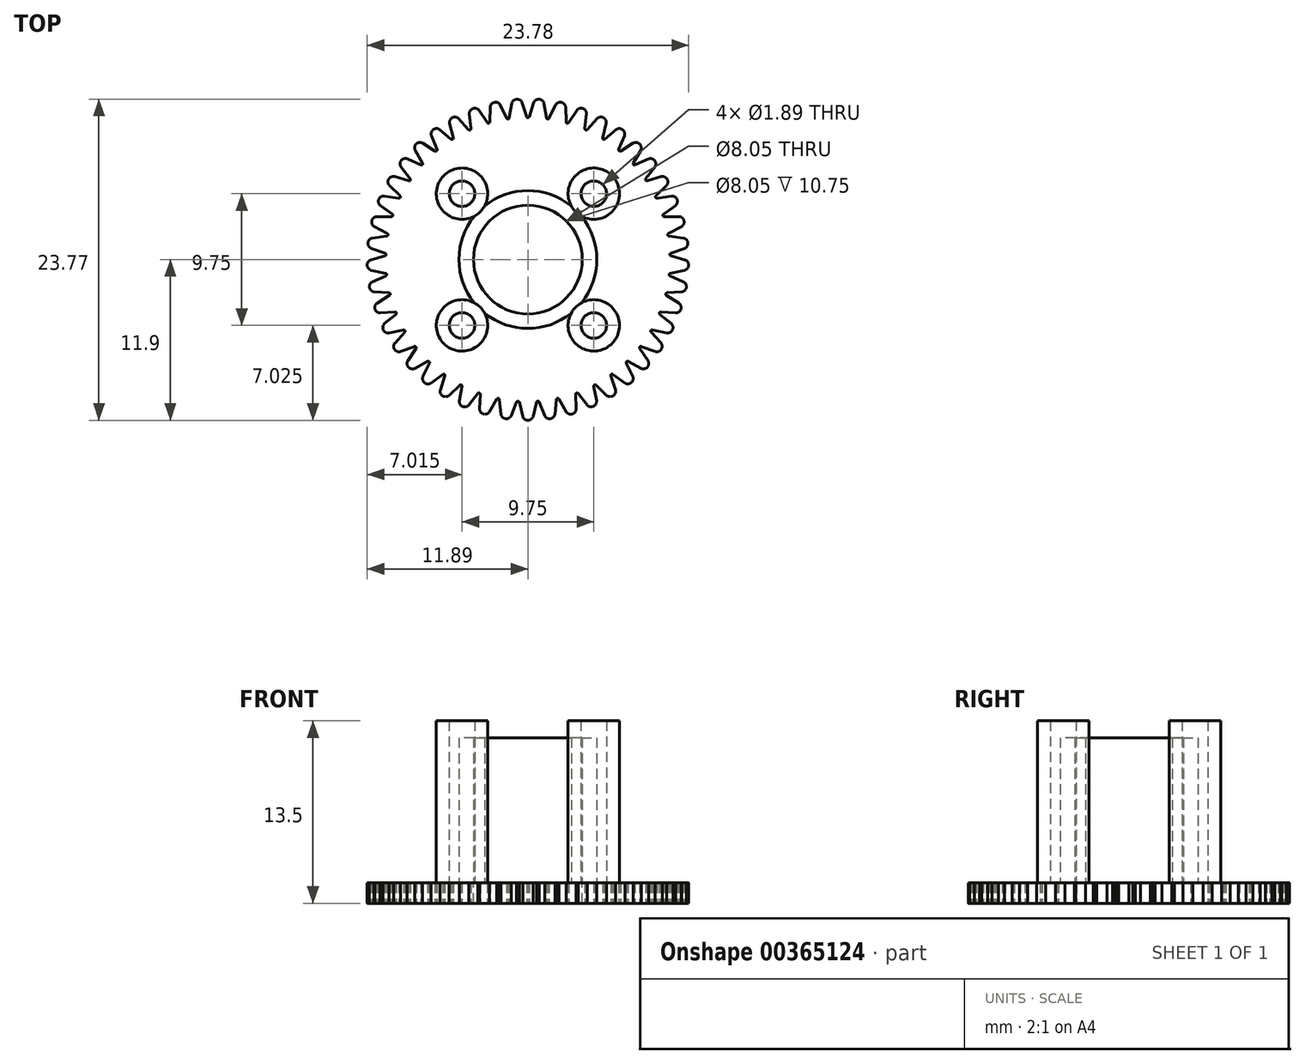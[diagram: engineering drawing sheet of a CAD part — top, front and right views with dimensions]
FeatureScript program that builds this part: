
annotation { "Feature Type Name" : "Feature", "Feature Type Description" : "" }
export const myFeature = defineFeature(function(context is Context, id is Id, definition is map)
    precondition{}
    {
        {
            var Q0;
            Q0=qCreatedBy(makeId("Top.planeOp"),FACE);
            var sketch = newSketch(context, id + "F0", { "sketchPlane" : qUnion([Q0])});
            skLineSegment(sketch, "E0.bottom", {"start": v(-6.77, 6.78) * mm, "end": v(6.78, 6.78) * mm});
            skLineSegment(sketch, "E0.top", {"start": v(-6.78, -6.78) * mm, "end": v(6.77, -6.78) * mm});
            skLineSegment(sketch, "E0.left", {"start": v(-6.77, 6.78) * mm, "end": v(-6.78, -6.78) * mm});
            skLineSegment(sketch, "E0.right", {"start": v(6.78, 6.78) * mm, "end": v(6.77, -6.78) * mm});
            skPoint(sketch, "E0.middle", {"position": v(0, 0) * mm});
            skCircle(sketch, "E1", {"center": v(-4.88, -4.88) * mm, "radius": 1.9 * mm});
            skCircle(sketch, "E2", {"center": v(-4.88, 4.88) * mm, "radius": 1.9 * mm});
            skCircle(sketch, "E3", {"center": v(4.88, 4.88) * mm, "radius": 1.9 * mm});
            skCircle(sketch, "E4", {"center": v(4.88, -4.88) * mm, "radius": 1.9 * mm});
            skCircle(sketch, "E5", {"center": v(0, 0) * mm, "radius": 5.1 * mm});
            skCircle(sketch, "E6", {"center": v(0, 0) * mm, "radius": 4.03 * mm});
            skCircle(sketch, "E7", {"center": v(-4.88, -4.88) * mm, "radius": 0.94 * mm});
            skCircle(sketch, "E8", {"center": v(-4.88, 4.88) * mm, "radius": 0.94 * mm});
            skCircle(sketch, "E9", {"center": v(4.88, 4.88) * mm, "radius": 0.94 * mm});
            skCircle(sketch, "E10", {"center": v(4.88, -4.88) * mm, "radius": 0.94 * mm});
            skSolve(sketch);
        }
        {
            var Q0;
            Q0=makeQuery(id+"F0.imprint","IMPRINT",FACE,{"disambiguationData":[TD([[makeQuery(id+"F0.imprint","IMPRINT",EDGE,{"derivedFrom":sQuery(id+"F0.wireOp",EDGE,"E8")}),-1.0]])]});
            var Q1;
            Q1=makeQuery(id+"F0.imprint","IMPRINT",FACE,{"disambiguationData":[TD([[makeQuery(id+"F0.imprint","IMPRINT",EDGE,{"derivedFrom":sQuery(id+"F0.wireOp",EDGE,"E9")}),-1.0]])]});
            var Q2;
            Q2=makeQuery(id+"F0.imprint","IMPRINT",FACE,{"disambiguationData":[TD([[makeQuery(id+"F0.imprint","IMPRINT",EDGE,{"derivedFrom":sQuery(id+"F0.wireOp",EDGE,"E10")}),-1.0]])]});
            var Q3;
            Q3=makeQuery(id+"F0.imprint","IMPRINT",FACE,{"disambiguationData":[TD([[makeQuery(id+"F0.imprint","IMPRINT",EDGE,{"derivedFrom":sQuery(id+"F0.wireOp",EDGE,"E7")}),-1.0]])]});
            var Q4;
            Q4=makeQuery(id+"F0.imprint","IMPRINT",FACE,{"disambiguationData":[TD([[makeQuery(id+"F0.imprint","IMPRINT",EDGE,{"derivedFrom":sQuery(id+"F0.wireOp",EDGE,"E6")}),-1.0]])]});
            var Q5;
            {var subQ0=sQuery(id+"F0.wireOp",EDGE,"E5");var subQ1=sQuery(id+"F0.wireOp",EDGE,"E2");var subQ2=makeQuery(id+"F0.imprint","INTERSECT",VERTEX,{"disambiguationData":[OD(0.0)],"derivedFrom":[subQ1,subQ0]});Q5=makeQuery(id+"F0.imprint","IMPRINT",FACE,{"disambiguationData":[TD([[makeQuery(id+"F0.imprint","IMPRINT",EDGE,{"disambiguationData":[TD([[subQ2,-1.0]])],"derivedFrom":subQ1}),1.0]])]});}
            var Q6;
            {var subQ0=sQuery(id+"F0.wireOp",EDGE,"E5");var subQ1=sQuery(id+"F0.wireOp",EDGE,"E3");var subQ2=makeQuery(id+"F0.imprint","INTERSECT",VERTEX,{"disambiguationData":[OD(0.0)],"derivedFrom":[subQ1,subQ0]});Q6=makeQuery(id+"F0.imprint","IMPRINT",FACE,{"disambiguationData":[TD([[makeQuery(id+"F0.imprint","IMPRINT",EDGE,{"disambiguationData":[TD([[subQ2,-1.0]])],"derivedFrom":subQ1}),1.0]])]});}
            var Q7;
            {var subQ0=sQuery(id+"F0.wireOp",EDGE,"E5");var subQ1=sQuery(id+"F0.wireOp",EDGE,"E4");var subQ2=makeQuery(id+"F0.imprint","INTERSECT",VERTEX,{"disambiguationData":[OD(0.0)],"derivedFrom":[subQ1,subQ0]});Q7=makeQuery(id+"F0.imprint","IMPRINT",FACE,{"disambiguationData":[TD([[makeQuery(id+"F0.imprint","IMPRINT",EDGE,{"disambiguationData":[TD([[subQ2,-1.0]])],"derivedFrom":subQ1}),1.0]])]});}
            var Q8;
            {var subQ0=sQuery(id+"F0.wireOp",EDGE,"E5");var subQ1=sQuery(id+"F0.wireOp",EDGE,"E1");var subQ2=makeQuery(id+"F0.imprint","INTERSECT",VERTEX,{"disambiguationData":[OD(0.0)],"derivedFrom":[subQ1,subQ0]});Q8=makeQuery(id+"F0.imprint","IMPRINT",FACE,{"disambiguationData":[TD([[makeQuery(id+"F0.imprint","IMPRINT",EDGE,{"disambiguationData":[TD([[subQ2,1.0]])],"derivedFrom":subQ1}),1.0]])]});}
            extrude(context, id + "F1", {"entities" : qUnion([Q0, Q1, Q2, Q3, Q4, Q5, Q6, Q7, Q8]), "depth" : 12 * mm});
        }
        {
            var Q0;
            Q0=makeQuery(id+"F1.opExtrude","CAP_FACE",FACE,{"disambiguationData":[OSD([sQuery(id+"F0.wireOp",EDGE,"E1"),sQuery(id+"F0.wireOp",EDGE,"E2"),sQuery(id+"F0.wireOp",EDGE,"E3"),sQuery(id+"F0.wireOp",EDGE,"E4"),sQuery(id+"F0.wireOp",EDGE,"E5"),sQuery(id+"F0.wireOp",EDGE,"E6")])],"isStart":true});
            var sketch = newSketch(context, id + "F2", { "sketchPlane" : qUnion([Q0])});
            skCircle(sketch, "E11", {"center": v(0, 0) * mm, "radius": 11.9 * mm});
            skSolve(sketch);
        }
        {
            var Q0;
            Q0 = qSketchRegion(id + "F2", true);
            extrude(context, id + "F3", {"entities" : qUnion([Q0]), "depth" : 1.5 * mm});
        }
        {
            var Q0;
            Q0=makeQuery(id+"F3.opExtrude","CAP_FACE",FACE,{"disambiguationData":[OSD([sQuery(id+"F2.wireOp",EDGE,"E11")])],"isStart":false});
            var sketch = newSketch(context, id + "F4", { "sketchPlane" : qUnion([Q0])});
            skLineSegment(sketch, "E12", {"start": v(-0.75, 10.47) * mm, "end": v(0.75, 10.47) * mm});
            skPoint(sketch, "E13", {"position": v(0, 10.47) * mm});
            skLineSegment(sketch, "E14", {"start": v(-0.4, 11.47) * mm, "end": v(0.4, 11.47) * mm});
            skPoint(sketch, "E15", {"position": v(0, 11.47) * mm});
            skArc(sketch, "E16", {"start": v(0.38, 11.62) * mm, "mid": v(0, 11.9) * mm, "end": v(-0.38, 11.62) * mm});
            skLineSegment(sketch, "E17.MirrorCS", {"start": v(0.64, 10.56) * mm, "end": v(0.38, 11.62) * mm});
            skLineSegment(sketch, "E18.MirrorCS", {"start": v(-0.64, 10.56) * mm, "end": v(-0.38, 11.62) * mm});
            skCircle(sketch, "E19.0", {"center": v(0, 0) * mm, "radius": 11.9 * mm});
            skCircle(sketch, "E20", {"center": v(0, 0) * mm, "radius": 12.27 * mm});
            skLineSegment(sketch, "E21", {"start": v(0, 0) * mm, "end": v(0, 10.47) * mm});
            skArc(sketch, "E22.MirrorCS", {"start": v(0.75, 10.47) * mm, "mid": v(0.68, 10.5) * mm, "end": v(0.64, 10.56) * mm});
            skArc(sketch, "E23", {"start": v(-0.75, 10.47) * mm, "mid": v(-0.67, 10.5) * mm, "end": v(-0.63, 10.58) * mm});
            skArc(sketch, "E24.1.0", {"start": v(-1.24, 11.56) * mm, "mid": v(-1.65, 11.78) * mm, "end": v(-2, 11.45) * mm});
            skLineSegment(sketch, "E24.1.1", {"start": v(-2.1, 10.37) * mm, "end": v(-2, 11.45) * mm});
            skLineSegment(sketch, "E24.1.2", {"start": v(-0.84, 10.55) * mm, "end": v(-1.24, 11.56) * mm});
            skArc(sketch, "E24.1.3", {"start": v(-2.2, 10.27) * mm, "mid": v(-2.13, 10.3) * mm, "end": v(-2.1, 10.39) * mm});
            skArc(sketch, "E24.1.4", {"start": v(-0.71, 10.48) * mm, "mid": v(-0.79, 10.5) * mm, "end": v(-0.84, 10.55) * mm});
            skArc(sketch, "E24.2.0", {"start": v(-2.84, 11.27) * mm, "mid": v(-3.28, 11.44) * mm, "end": v(-3.57, 11.07) * mm});
            skLineSegment(sketch, "E24.2.1", {"start": v(-3.53, 9.98) * mm, "end": v(-3.57, 11.07) * mm});
            skLineSegment(sketch, "E24.2.2", {"start": v(-2.3, 10.33) * mm, "end": v(-2.84, 11.27) * mm});
            skArc(sketch, "E24.2.3", {"start": v(-3.6, 9.86) * mm, "mid": v(-3.54, 9.91) * mm, "end": v(-3.53, 10) * mm});
            skArc(sketch, "E24.2.4", {"start": v(-2.17, 10.27) * mm, "mid": v(-2.24, 10.28) * mm, "end": v(-2.3, 10.33) * mm});
            skArc(sketch, "E24.3.0", {"start": v(-4.38, 10.77) * mm, "mid": v(-4.84, 10.87) * mm, "end": v(-5.07, 10.46) * mm});
            skLineSegment(sketch, "E24.3.1", {"start": v(-4.88, 9.39) * mm, "end": v(-5.07, 10.46) * mm});
            skLineSegment(sketch, "E24.3.2", {"start": v(-3.71, 9.9) * mm, "end": v(-4.38, 10.77) * mm});
            skArc(sketch, "E24.3.3", {"start": v(-4.95, 9.26) * mm, "mid": v(-4.89, 9.32) * mm, "end": v(-4.88, 9.4) * mm});
            skArc(sketch, "E24.3.4", {"start": v(-3.57, 9.87) * mm, "mid": v(-3.65, 9.87) * mm, "end": v(-3.71, 9.9) * mm});
            skArc(sketch, "E24.4.0", {"start": v(-5.83, 10.06) * mm, "mid": v(-6.3, 10.1) * mm, "end": v(-6.48, 9.65) * mm});
            skLineSegment(sketch, "E24.4.1", {"start": v(-6.14, 8.62) * mm, "end": v(-6.48, 9.65) * mm});
            skLineSegment(sketch, "E24.4.2", {"start": v(-5.05, 9.3) * mm, "end": v(-5.83, 10.06) * mm});
            skArc(sketch, "E24.4.3", {"start": v(-6.19, 8.48) * mm, "mid": v(-6.14, 8.55) * mm, "end": v(-6.14, 8.63) * mm});
            skArc(sketch, "E24.4.4", {"start": v(-4.91, 9.28) * mm, "mid": v(-4.99, 9.27) * mm, "end": v(-5.05, 9.3) * mm});
            skArc(sketch, "E24.5.0", {"start": v(-7.18, 9.15) * mm, "mid": v(-7.65, 9.11) * mm, "end": v(-7.76, 8.66) * mm});
            skLineSegment(sketch, "E24.5.1", {"start": v(-7.28, 7.68) * mm, "end": v(-7.76, 8.66) * mm});
            skLineSegment(sketch, "E24.5.2", {"start": v(-6.3, 8.5) * mm, "end": v(-7.18, 9.15) * mm});
            skArc(sketch, "E24.5.3", {"start": v(-7.3, 7.54) * mm, "mid": v(-7.27, 7.61) * mm, "end": v(-7.29, 7.7) * mm});
            skArc(sketch, "E24.5.4", {"start": v(-6.16, 8.5) * mm, "mid": v(-6.23, 8.48) * mm, "end": v(-6.3, 8.5) * mm});
            skArc(sketch, "E24.6.0", {"start": v(-8.38, 8.06) * mm, "mid": v(-8.84, 7.96) * mm, "end": v(-8.9, 7.5) * mm});
            skLineSegment(sketch, "E24.6.1", {"start": v(-8.28, 6.6) * mm, "end": v(-8.9, 7.5) * mm});
            skLineSegment(sketch, "E24.6.2", {"start": v(-7.42, 7.54) * mm, "end": v(-8.38, 8.06) * mm});
            skArc(sketch, "E24.6.3", {"start": v(-8.29, 6.45) * mm, "mid": v(-8.26, 6.53) * mm, "end": v(-8.29, 6.6) * mm});
            skArc(sketch, "E24.6.4", {"start": v(-7.28, 7.57) * mm, "mid": v(-7.35, 7.53) * mm, "end": v(-7.42, 7.54) * mm});
            skArc(sketch, "E24.7.0", {"start": v(-9.42, 6.81) * mm, "mid": v(-9.86, 6.65) * mm, "end": v(-9.85, 6.18) * mm});
            skLineSegment(sketch, "E24.7.1", {"start": v(-9.11, 5.38) * mm, "end": v(-9.85, 6.18) * mm});
            skLineSegment(sketch, "E24.7.2", {"start": v(-8.4, 6.44) * mm, "end": v(-9.42, 6.81) * mm});
            skArc(sketch, "E24.7.3", {"start": v(-9.1, 5.24) * mm, "mid": v(-9.09, 5.32) * mm, "end": v(-9.12, 5.39) * mm});
            skArc(sketch, "E24.7.4", {"start": v(-8.26, 6.48) * mm, "mid": v(-8.32, 6.44) * mm, "end": v(-8.4, 6.44) * mm});
            skArc(sketch, "E24.8.0", {"start": v(-10.28, 5.44) * mm, "mid": v(-10.7, 5.22) * mm, "end": v(-10.61, 4.75) * mm});
            skLineSegment(sketch, "E24.8.1", {"start": v(-9.77, 4.06) * mm, "end": v(-10.61, 4.75) * mm});
            skLineSegment(sketch, "E24.8.2", {"start": v(-9.21, 5.2) * mm, "end": v(-10.28, 5.44) * mm});
            skArc(sketch, "E24.8.3", {"start": v(-9.74, 3.92) * mm, "mid": v(-9.74, 4) * mm, "end": v(-9.79, 4.07) * mm});
            skArc(sketch, "E24.8.4", {"start": v(-9.09, 5.27) * mm, "mid": v(-9.14, 5.22) * mm, "end": v(-9.21, 5.2) * mm});
            skArc(sketch, "E24.9.0", {"start": v(-10.93, 3.95) * mm, "mid": v(-11.32, 3.68) * mm, "end": v(-11.17, 3.23) * mm});
            skLineSegment(sketch, "E24.9.1", {"start": v(-10.24, 2.66) * mm, "end": v(-11.17, 3.23) * mm});
            skLineSegment(sketch, "E24.9.2", {"start": v(-9.85, 3.87) * mm, "end": v(-10.93, 3.95) * mm});
            skArc(sketch, "E24.9.3", {"start": v(-10.2, 2.52) * mm, "mid": v(-10.2, 2.6) * mm, "end": v(-10.26, 2.66) * mm});
            skArc(sketch, "E24.9.4", {"start": v(-9.73, 3.95) * mm, "mid": v(-9.78, 3.9) * mm, "end": v(-9.85, 3.87) * mm});
            skArc(sketch, "E24.10.0", {"start": v(-11.38, 2.4) * mm, "mid": v(-11.72, 2.07) * mm, "end": v(-11.51, 1.64) * mm});
            skLineSegment(sketch, "E24.10.1", {"start": v(-10.51, 1.2) * mm, "end": v(-11.51, 1.64) * mm});
            skLineSegment(sketch, "E24.10.2", {"start": v(-10.29, 2.46) * mm, "end": v(-11.38, 2.4) * mm});
            skArc(sketch, "E24.10.3", {"start": v(-10.44, 1.08) * mm, "mid": v(-10.46, 1.16) * mm, "end": v(-10.53, 1.21) * mm});
            skArc(sketch, "E24.10.4", {"start": v(-10.18, 2.56) * mm, "mid": v(-10.22, 2.5) * mm, "end": v(-10.29, 2.46) * mm});
            skArc(sketch, "E24.11.0", {"start": v(-11.6, 0.79) * mm, "mid": v(-11.9, 0.42) * mm, "end": v(-11.63, 0.02) * mm});
            skLineSegment(sketch, "E24.11.1", {"start": v(-10.58, -0.27) * mm, "end": v(-11.63, 0.02) * mm});
            skLineSegment(sketch, "E24.11.2", {"start": v(-10.53, 1) * mm, "end": v(-11.6, 0.79) * mm});
            skArc(sketch, "E24.11.3", {"start": v(-10.5, -0.38) * mm, "mid": v(-10.52, -0.3) * mm, "end": v(-10.6, -0.27) * mm});
            skArc(sketch, "E24.11.4", {"start": v(-10.44, 1.12) * mm, "mid": v(-10.47, 1.05) * mm, "end": v(-10.53, 1) * mm});
            skArc(sketch, "E24.12.0", {"start": v(-11.6, -0.83) * mm, "mid": v(-11.83, -1.24) * mm, "end": v(-11.52, -1.6) * mm});
            skLineSegment(sketch, "E24.12.1", {"start": v(-10.44, -1.74) * mm, "end": v(-11.52, -1.6) * mm});
            skLineSegment(sketch, "E24.12.2", {"start": v(-10.57, -0.47) * mm, "end": v(-11.6, -0.83) * mm});
            skArc(sketch, "E24.12.3", {"start": v(-10.34, -1.84) * mm, "mid": v(-10.38, -1.77) * mm, "end": v(-10.45, -1.74) * mm});
            skArc(sketch, "E24.12.4", {"start": v(-10.5, -0.35) * mm, "mid": v(-10.51, -0.42) * mm, "end": v(-10.57, -0.47) * mm});
            skArc(sketch, "E24.13.0", {"start": v(-11.37, -2.44) * mm, "mid": v(-11.54, -2.88) * mm, "end": v(-11.18, -3.18) * mm});
            skLineSegment(sketch, "E24.13.1", {"start": v(-10.1, -3.17) * mm, "end": v(-11.18, -3.18) * mm});
            skLineSegment(sketch, "E24.13.2", {"start": v(-10.4, -1.93) * mm, "end": v(-11.37, -2.44) * mm});
            skArc(sketch, "E24.13.3", {"start": v(-9.98, -3.26) * mm, "mid": v(-10.03, -3.2) * mm, "end": v(-10.1, -3.17) * mm});
            skArc(sketch, "E24.13.4", {"start": v(-10.34, -1.8) * mm, "mid": v(-10.35, -1.88) * mm, "end": v(-10.4, -1.93) * mm});
            skArc(sketch, "E24.14.0", {"start": v(-10.92, -4) * mm, "mid": v(-11.03, -4.46) * mm, "end": v(-10.63, -4.7) * mm});
            skLineSegment(sketch, "E24.14.1", {"start": v(-9.55, -4.55) * mm, "end": v(-10.63, -4.7) * mm});
            skLineSegment(sketch, "E24.14.2", {"start": v(-10.03, -3.36) * mm, "end": v(-10.92, -4) * mm});
            skArc(sketch, "E24.14.3", {"start": v(-9.43, -4.62) * mm, "mid": v(-9.49, -4.56) * mm, "end": v(-9.57, -4.55) * mm});
            skArc(sketch, "E24.14.4", {"start": v(-10, -3.23) * mm, "mid": v(-10, -3.3) * mm, "end": v(-10.03, -3.36) * mm});
            skArc(sketch, "E24.15.0", {"start": v(-10.25, -5.48) * mm, "mid": v(-10.3, -5.95) * mm, "end": v(-9.87, -6.14) * mm});
            skLineSegment(sketch, "E24.15.1", {"start": v(-8.83, -5.83) * mm, "end": v(-9.87, -6.14) * mm});
            skLineSegment(sketch, "E24.15.2", {"start": v(-9.47, -4.73) * mm, "end": v(-10.25, -5.48) * mm});
            skArc(sketch, "E24.15.3", {"start": v(-8.7, -5.89) * mm, "mid": v(-8.76, -5.84) * mm, "end": v(-8.84, -5.84) * mm});
            skArc(sketch, "E24.15.4", {"start": v(-9.45, -4.59) * mm, "mid": v(-9.43, -4.66) * mm, "end": v(-9.47, -4.73) * mm});
            skArc(sketch, "E24.16.0", {"start": v(-9.4, -6.85) * mm, "mid": v(-9.38, -7.32) * mm, "end": v(-8.92, -7.45) * mm});
            skLineSegment(sketch, "E24.16.1", {"start": v(-7.93, -7) * mm, "end": v(-8.92, -7.45) * mm});
            skLineSegment(sketch, "E24.16.2", {"start": v(-8.72, -6) * mm, "end": v(-9.4, -6.85) * mm});
            skArc(sketch, "E24.16.3", {"start": v(-7.8, -7.04) * mm, "mid": v(-7.86, -7) * mm, "end": v(-7.94, -7.01) * mm});
            skArc(sketch, "E24.16.4", {"start": v(-8.72, -5.86) * mm, "mid": v(-8.7, -5.93) * mm, "end": v(-8.72, -6) * mm});
            skArc(sketch, "E24.17.0", {"start": v(-8.35, -8.1) * mm, "mid": v(-8.27, -8.56) * mm, "end": v(-7.8, -8.62) * mm});
            skLineSegment(sketch, "E24.17.1", {"start": v(-6.88, -8.04) * mm, "end": v(-7.8, -8.62) * mm});
            skLineSegment(sketch, "E24.17.2", {"start": v(-7.8, -7.15) * mm, "end": v(-8.35, -8.1) * mm});
            skArc(sketch, "E24.17.3", {"start": v(-6.74, -8.06) * mm, "mid": v(-6.81, -8.03) * mm, "end": v(-6.9, -8.05) * mm});
            skArc(sketch, "E24.17.4", {"start": v(-7.82, -7.01) * mm, "mid": v(-7.78, -7.08) * mm, "end": v(-7.8, -7.15) * mm});
            skArc(sketch, "E24.18.0", {"start": v(-7.14, -9.18) * mm, "mid": v(-7, -9.63) * mm, "end": v(-6.52, -9.63) * mm});
            skLineSegment(sketch, "E24.18.1", {"start": v(-5.7, -8.92) * mm, "end": v(-6.52, -9.63) * mm});
            skLineSegment(sketch, "E24.18.2", {"start": v(-6.72, -8.17) * mm, "end": v(-7.14, -9.18) * mm});
            skArc(sketch, "E24.18.3", {"start": v(-5.55, -8.91) * mm, "mid": v(-5.63, -8.9) * mm, "end": v(-5.7, -8.93) * mm});
            skArc(sketch, "E24.18.4", {"start": v(-6.76, -8.03) * mm, "mid": v(-6.72, -8.1) * mm, "end": v(-6.72, -8.17) * mm});
            skArc(sketch, "E24.19.0", {"start": v(-5.8, -10.08) * mm, "mid": v(-5.59, -10.5) * mm, "end": v(-5.12, -10.44) * mm});
            skLineSegment(sketch, "E24.19.1", {"start": v(-4.4, -9.62) * mm, "end": v(-5.12, -10.44) * mm});
            skLineSegment(sketch, "E24.19.2", {"start": v(-5.52, -9.02) * mm, "end": v(-5.8, -10.08) * mm});
            skArc(sketch, "E24.19.3", {"start": v(-4.25, -9.6) * mm, "mid": v(-4.34, -9.6) * mm, "end": v(-4.4, -9.64) * mm});
            skArc(sketch, "E24.19.4", {"start": v(-5.58, -8.9) * mm, "mid": v(-5.53, -8.95) * mm, "end": v(-5.52, -9.02) * mm});
            skArc(sketch, "E24.20.0", {"start": v(-4.33, -10.79) * mm, "mid": v(-4.07, -11.18) * mm, "end": v(-3.62, -11.05) * mm});
            skLineSegment(sketch, "E24.20.1", {"start": v(-3.01, -10.14) * mm, "end": v(-3.62, -11.05) * mm});
            skLineSegment(sketch, "E24.20.2", {"start": v(-4.21, -9.7) * mm, "end": v(-4.33, -10.79) * mm});
            skArc(sketch, "E24.20.3", {"start": v(-2.88, -10.1) * mm, "mid": v(-2.96, -10.1) * mm, "end": v(-3.02, -10.16) * mm});
            skArc(sketch, "E24.20.4", {"start": v(-4.29, -9.59) * mm, "mid": v(-4.23, -9.63) * mm, "end": v(-4.21, -9.7) * mm});
            skArc(sketch, "E24.21.0", {"start": v(-2.79, -11.29) * mm, "mid": v(-2.47, -11.64) * mm, "end": v(-2.04, -11.45) * mm});
            skLineSegment(sketch, "E24.21.1", {"start": v(-1.57, -10.46) * mm, "end": v(-2.04, -11.45) * mm});
            skLineSegment(sketch, "E24.21.2", {"start": v(-2.82, -10.2) * mm, "end": v(-2.79, -11.29) * mm});
            skArc(sketch, "E24.21.3", {"start": v(-1.44, -10.4) * mm, "mid": v(-1.52, -10.42) * mm, "end": v(-1.58, -10.48) * mm});
            skArc(sketch, "E24.21.4", {"start": v(-2.91, -10.09) * mm, "mid": v(-2.85, -10.13) * mm, "end": v(-2.82, -10.2) * mm});
            skArc(sketch, "E24.22.0", {"start": v(-1.2, -11.56) * mm, "mid": v(-0.83, -11.87) * mm, "end": v(-0.43, -11.62) * mm});
            skLineSegment(sketch, "E24.22.1", {"start": v(-0.1, -10.58) * mm, "end": v(-0.43, -11.62) * mm});
            skLineSegment(sketch, "E24.22.2", {"start": v(-1.37, -10.5) * mm, "end": v(-1.2, -11.56) * mm});
            skArc(sketch, "E24.22.3", {"start": v(0.02, -10.5) * mm, "mid": v(-0.06, -10.53) * mm, "end": v(-0.1, -10.6) * mm});
            skArc(sketch, "E24.22.4", {"start": v(-1.48, -10.4) * mm, "mid": v(-1.41, -10.43) * mm, "end": v(-1.37, -10.5) * mm});
            skArc(sketch, "E24.23.0", {"start": v(0.43, -11.62) * mm, "mid": v(0.83, -11.87) * mm, "end": v(1.2, -11.57) * mm});
            skLineSegment(sketch, "E24.23.1", {"start": v(1.37, -10.5) * mm, "end": v(1.2, -11.57) * mm});
            skLineSegment(sketch, "E24.23.2", {"start": v(0.1, -10.58) * mm, "end": v(0.43, -11.62) * mm});
            skArc(sketch, "E24.23.3", {"start": v(1.48, -10.4) * mm, "mid": v(1.4, -10.43) * mm, "end": v(1.37, -10.5) * mm});
            skArc(sketch, "E24.23.4", {"start": v(-0.02, -10.5) * mm, "mid": v(0.05, -10.52) * mm, "end": v(0.1, -10.58) * mm});
            skArc(sketch, "E24.24.0", {"start": v(2.04, -11.44) * mm, "mid": v(2.47, -11.64) * mm, "end": v(2.79, -11.29) * mm});
            skLineSegment(sketch, "E24.24.1", {"start": v(2.82, -10.2) * mm, "end": v(2.79, -11.29) * mm});
            skLineSegment(sketch, "E24.24.2", {"start": v(1.57, -10.46) * mm, "end": v(2.04, -11.44) * mm});
            skArc(sketch, "E24.24.3", {"start": v(2.91, -10.09) * mm, "mid": v(2.84, -10.14) * mm, "end": v(2.82, -10.21) * mm});
            skArc(sketch, "E24.24.4", {"start": v(1.44, -10.4) * mm, "mid": v(1.52, -10.41) * mm, "end": v(1.57, -10.46) * mm});
            skArc(sketch, "E24.25.0", {"start": v(3.62, -11.05) * mm, "mid": v(4.07, -11.18) * mm, "end": v(4.33, -10.79) * mm});
            skLineSegment(sketch, "E24.25.1", {"start": v(4.21, -9.7) * mm, "end": v(4.33, -10.79) * mm});
            skLineSegment(sketch, "E24.25.2", {"start": v(3.01, -10.14) * mm, "end": v(3.62, -11.05) * mm});
            skArc(sketch, "E24.25.3", {"start": v(4.29, -9.59) * mm, "mid": v(4.23, -9.64) * mm, "end": v(4.21, -9.72) * mm});
            skArc(sketch, "E24.25.4", {"start": v(2.88, -10.1) * mm, "mid": v(2.95, -10.1) * mm, "end": v(3.01, -10.14) * mm});
            skArc(sketch, "E24.26.0", {"start": v(5.12, -10.44) * mm, "mid": v(5.58, -10.5) * mm, "end": v(5.8, -10.08) * mm});
            skLineSegment(sketch, "E24.26.1", {"start": v(5.52, -9.02) * mm, "end": v(5.8, -10.08) * mm});
            skLineSegment(sketch, "E24.26.2", {"start": v(4.4, -9.62) * mm, "end": v(5.12, -10.44) * mm});
            skArc(sketch, "E24.26.3", {"start": v(5.58, -8.9) * mm, "mid": v(5.53, -8.96) * mm, "end": v(5.53, -9.04) * mm});
            skArc(sketch, "E24.26.4", {"start": v(4.25, -9.6) * mm, "mid": v(4.33, -9.6) * mm, "end": v(4.4, -9.62) * mm});
            skArc(sketch, "E24.27.0", {"start": v(6.52, -9.62) * mm, "mid": v(7, -9.63) * mm, "end": v(7.14, -9.18) * mm});
            skLineSegment(sketch, "E24.27.1", {"start": v(6.72, -8.17) * mm, "end": v(7.14, -9.18) * mm});
            skLineSegment(sketch, "E24.27.2", {"start": v(5.7, -8.92) * mm, "end": v(6.52, -9.62) * mm});
            skArc(sketch, "E24.27.3", {"start": v(6.76, -8.03) * mm, "mid": v(6.72, -8.1) * mm, "end": v(6.73, -8.18) * mm});
            skArc(sketch, "E24.27.4", {"start": v(5.55, -8.91) * mm, "mid": v(5.62, -8.9) * mm, "end": v(5.7, -8.92) * mm});
            skArc(sketch, "E24.28.0", {"start": v(7.8, -8.62) * mm, "mid": v(8.26, -8.56) * mm, "end": v(8.35, -8.1) * mm});
            skLineSegment(sketch, "E24.28.1", {"start": v(7.8, -7.15) * mm, "end": v(8.35, -8.1) * mm});
            skLineSegment(sketch, "E24.28.2", {"start": v(6.88, -8.04) * mm, "end": v(7.8, -8.62) * mm});
            skArc(sketch, "E24.28.3", {"start": v(7.82, -7.01) * mm, "mid": v(7.78, -7.09) * mm, "end": v(7.8, -7.17) * mm});
            skArc(sketch, "E24.28.4", {"start": v(6.74, -8.06) * mm, "mid": v(6.8, -8.03) * mm, "end": v(6.88, -8.04) * mm});
            skArc(sketch, "E24.29.0", {"start": v(8.92, -7.45) * mm, "mid": v(9.38, -7.33) * mm, "end": v(9.4, -6.85) * mm});
            skLineSegment(sketch, "E24.29.1", {"start": v(8.72, -6) * mm, "end": v(9.4, -6.85) * mm});
            skLineSegment(sketch, "E24.29.2", {"start": v(7.93, -7) * mm, "end": v(8.92, -7.45) * mm});
            skArc(sketch, "E24.29.3", {"start": v(8.72, -5.86) * mm, "mid": v(8.7, -5.94) * mm, "end": v(8.73, -6.01) * mm});
            skArc(sketch, "E24.29.4", {"start": v(7.8, -7.04) * mm, "mid": v(7.85, -7) * mm, "end": v(7.93, -7) * mm});
            skArc(sketch, "E24.30.0", {"start": v(9.87, -6.14) * mm, "mid": v(10.3, -5.95) * mm, "end": v(10.25, -5.48) * mm});
            skLineSegment(sketch, "E24.30.1", {"start": v(9.47, -4.73) * mm, "end": v(10.25, -5.48) * mm});
            skLineSegment(sketch, "E24.30.2", {"start": v(8.83, -5.83) * mm, "end": v(9.87, -6.14) * mm});
            skArc(sketch, "E24.30.3", {"start": v(9.45, -4.59) * mm, "mid": v(9.44, -4.67) * mm, "end": v(9.48, -4.74) * mm});
            skArc(sketch, "E24.30.4", {"start": v(8.7, -5.89) * mm, "mid": v(8.75, -5.84) * mm, "end": v(8.83, -5.83) * mm});
            skArc(sketch, "E24.31.0", {"start": v(10.63, -4.7) * mm, "mid": v(11.03, -4.46) * mm, "end": v(10.92, -4) * mm});
            skLineSegment(sketch, "E24.31.1", {"start": v(10.03, -3.36) * mm, "end": v(10.92, -4) * mm});
            skLineSegment(sketch, "E24.31.2", {"start": v(9.55, -4.55) * mm, "end": v(10.63, -4.7) * mm});
            skArc(sketch, "E24.31.3", {"start": v(10, -3.23) * mm, "mid": v(10, -3.31) * mm, "end": v(10.05, -3.37) * mm});
            skArc(sketch, "E24.31.4", {"start": v(9.43, -4.62) * mm, "mid": v(9.48, -4.56) * mm, "end": v(9.55, -4.55) * mm});
            skArc(sketch, "E24.32.0", {"start": v(11.18, -3.18) * mm, "mid": v(11.54, -2.88) * mm, "end": v(11.37, -2.44) * mm});
            skLineSegment(sketch, "E24.32.1", {"start": v(10.4, -1.93) * mm, "end": v(11.37, -2.44) * mm});
            skLineSegment(sketch, "E24.32.2", {"start": v(10.1, -3.17) * mm, "end": v(11.18, -3.18) * mm});
            skArc(sketch, "E24.32.3", {"start": v(10.34, -1.8) * mm, "mid": v(10.36, -1.89) * mm, "end": v(10.42, -1.94) * mm});
            skArc(sketch, "E24.32.4", {"start": v(9.98, -3.26) * mm, "mid": v(10.02, -3.2) * mm, "end": v(10.1, -3.17) * mm});
            skArc(sketch, "E24.33.0", {"start": v(11.52, -1.6) * mm, "mid": v(11.83, -1.24) * mm, "end": v(11.6, -0.84) * mm});
            skLineSegment(sketch, "E24.33.1", {"start": v(10.57, -0.47) * mm, "end": v(11.6, -0.84) * mm});
            skLineSegment(sketch, "E24.33.2", {"start": v(10.44, -1.74) * mm, "end": v(11.52, -1.6) * mm});
            skArc(sketch, "E24.33.3", {"start": v(10.5, -0.35) * mm, "mid": v(10.52, -0.43) * mm, "end": v(10.59, -0.47) * mm});
            skArc(sketch, "E24.33.4", {"start": v(10.34, -1.84) * mm, "mid": v(10.37, -1.77) * mm, "end": v(10.44, -1.74) * mm});
            skArc(sketch, "E24.34.0", {"start": v(11.62, 0.02) * mm, "mid": v(11.9, 0.41) * mm, "end": v(11.6, 0.79) * mm});
            skLineSegment(sketch, "E24.34.1", {"start": v(10.53, 1) * mm, "end": v(11.6, 0.79) * mm});
            skLineSegment(sketch, "E24.34.2", {"start": v(10.58, -0.27) * mm, "end": v(11.62, 0.02) * mm});
            skArc(sketch, "E24.34.3", {"start": v(10.44, 1.12) * mm, "mid": v(10.48, 1.04) * mm, "end": v(10.55, 1) * mm});
            skArc(sketch, "E24.34.4", {"start": v(10.5, -0.38) * mm, "mid": v(10.52, -0.31) * mm, "end": v(10.58, -0.27) * mm});
            skArc(sketch, "E24.35.0", {"start": v(11.5, 1.64) * mm, "mid": v(11.72, 2.07) * mm, "end": v(11.38, 2.4) * mm});
            skLineSegment(sketch, "E24.35.1", {"start": v(10.29, 2.46) * mm, "end": v(11.38, 2.4) * mm});
            skLineSegment(sketch, "E24.35.2", {"start": v(10.51, 1.2) * mm, "end": v(11.5, 1.64) * mm});
            skArc(sketch, "E24.35.3", {"start": v(10.18, 2.56) * mm, "mid": v(10.23, 2.49) * mm, "end": v(10.3, 2.46) * mm});
            skArc(sketch, "E24.35.4", {"start": v(10.44, 1.08) * mm, "mid": v(10.46, 1.15) * mm, "end": v(10.51, 1.2) * mm});
            skArc(sketch, "E24.36.0", {"start": v(11.17, 3.23) * mm, "mid": v(11.32, 3.68) * mm, "end": v(10.93, 3.95) * mm});
            skLineSegment(sketch, "E24.36.1", {"start": v(9.85, 3.87) * mm, "end": v(10.93, 3.95) * mm});
            skLineSegment(sketch, "E24.36.2", {"start": v(10.24, 2.66) * mm, "end": v(11.17, 3.23) * mm});
            skArc(sketch, "E24.36.3", {"start": v(9.73, 3.95) * mm, "mid": v(9.78, 3.89) * mm, "end": v(9.86, 3.87) * mm});
            skArc(sketch, "E24.36.4", {"start": v(10.2, 2.52) * mm, "mid": v(10.2, 2.6) * mm, "end": v(10.24, 2.66) * mm});
            skArc(sketch, "E24.37.0", {"start": v(10.61, 4.75) * mm, "mid": v(10.7, 5.21) * mm, "end": v(10.28, 5.44) * mm});
            skLineSegment(sketch, "E24.37.1", {"start": v(9.21, 5.2) * mm, "end": v(10.28, 5.44) * mm});
            skLineSegment(sketch, "E24.37.2", {"start": v(9.77, 4.06) * mm, "end": v(10.61, 4.75) * mm});
            skArc(sketch, "E24.37.3", {"start": v(9.09, 5.27) * mm, "mid": v(9.15, 5.21) * mm, "end": v(9.23, 5.2) * mm});
            skArc(sketch, "E24.37.4", {"start": v(9.74, 3.92) * mm, "mid": v(9.74, 4) * mm, "end": v(9.77, 4.06) * mm});
            skArc(sketch, "E24.38.0", {"start": v(9.85, 6.18) * mm, "mid": v(9.86, 6.65) * mm, "end": v(9.42, 6.81) * mm});
            skLineSegment(sketch, "E24.38.1", {"start": v(8.4, 6.44) * mm, "end": v(9.42, 6.81) * mm});
            skLineSegment(sketch, "E24.38.2", {"start": v(9.11, 5.38) * mm, "end": v(9.85, 6.18) * mm});
            skArc(sketch, "E24.38.3", {"start": v(8.26, 6.48) * mm, "mid": v(8.33, 6.43) * mm, "end": v(8.41, 6.44) * mm});
            skArc(sketch, "E24.38.4", {"start": v(9.1, 5.24) * mm, "mid": v(9.09, 5.3) * mm, "end": v(9.11, 5.38) * mm});
            skArc(sketch, "E24.39.0", {"start": v(8.89, 7.5) * mm, "mid": v(8.84, 7.96) * mm, "end": v(8.38, 8.06) * mm});
            skLineSegment(sketch, "E24.39.1", {"start": v(7.42, 7.54) * mm, "end": v(8.38, 8.06) * mm});
            skLineSegment(sketch, "E24.39.2", {"start": v(8.28, 6.6) * mm, "end": v(8.89, 7.5) * mm});
            skArc(sketch, "E24.39.3", {"start": v(7.28, 7.57) * mm, "mid": v(7.36, 7.53) * mm, "end": v(7.44, 7.55) * mm});
            skArc(sketch, "E24.39.4", {"start": v(8.29, 6.45) * mm, "mid": v(8.26, 6.52) * mm, "end": v(8.28, 6.6) * mm});
            skArc(sketch, "E24.40.0", {"start": v(7.76, 8.66) * mm, "mid": v(7.65, 9.11) * mm, "end": v(7.18, 9.15) * mm});
            skLineSegment(sketch, "E24.40.1", {"start": v(6.3, 8.5) * mm, "end": v(7.18, 9.15) * mm});
            skLineSegment(sketch, "E24.40.2", {"start": v(7.28, 7.68) * mm, "end": v(7.76, 8.66) * mm});
            skArc(sketch, "E24.40.3", {"start": v(6.16, 8.5) * mm, "mid": v(6.24, 8.48) * mm, "end": v(6.31, 8.51) * mm});
            skArc(sketch, "E24.40.4", {"start": v(7.3, 7.54) * mm, "mid": v(7.27, 7.6) * mm, "end": v(7.28, 7.68) * mm});
            skArc(sketch, "E24.41.0", {"start": v(6.48, 9.65) * mm, "mid": v(6.3, 10.09) * mm, "end": v(5.83, 10.06) * mm});
            skLineSegment(sketch, "E24.41.1", {"start": v(5.05, 9.3) * mm, "end": v(5.83, 10.06) * mm});
            skLineSegment(sketch, "E24.41.2", {"start": v(6.14, 8.62) * mm, "end": v(6.48, 9.65) * mm});
            skArc(sketch, "E24.41.3", {"start": v(4.91, 9.28) * mm, "mid": v(5, 9.27) * mm, "end": v(5.07, 9.3) * mm});
            skArc(sketch, "E24.41.4", {"start": v(6.19, 8.48) * mm, "mid": v(6.14, 8.54) * mm, "end": v(6.14, 8.62) * mm});
            skArc(sketch, "E24.42.0", {"start": v(5.07, 10.46) * mm, "mid": v(4.84, 10.87) * mm, "end": v(4.38, 10.77) * mm});
            skLineSegment(sketch, "E24.42.1", {"start": v(3.71, 9.9) * mm, "end": v(4.38, 10.77) * mm});
            skLineSegment(sketch, "E24.42.2", {"start": v(4.88, 9.39) * mm, "end": v(5.07, 10.46) * mm});
            skArc(sketch, "E24.42.3", {"start": v(3.57, 9.87) * mm, "mid": v(3.66, 9.87) * mm, "end": v(3.72, 9.92) * mm});
            skArc(sketch, "E24.42.4", {"start": v(4.95, 9.26) * mm, "mid": v(4.9, 9.32) * mm, "end": v(4.88, 9.39) * mm});
            skArc(sketch, "E24.43.0", {"start": v(3.57, 11.06) * mm, "mid": v(3.28, 11.44) * mm, "end": v(2.84, 11.28) * mm});
            skLineSegment(sketch, "E24.43.1", {"start": v(2.3, 10.33) * mm, "end": v(2.84, 11.28) * mm});
            skLineSegment(sketch, "E24.43.2", {"start": v(3.53, 9.98) * mm, "end": v(3.57, 11.06) * mm});
            skArc(sketch, "E24.43.3", {"start": v(2.17, 10.27) * mm, "mid": v(2.25, 10.28) * mm, "end": v(2.3, 10.34) * mm});
            skArc(sketch, "E24.43.4", {"start": v(3.6, 9.86) * mm, "mid": v(3.55, 9.9) * mm, "end": v(3.53, 9.98) * mm});
            skArc(sketch, "E24.44.0", {"start": v(2, 11.45) * mm, "mid": v(1.66, 11.78) * mm, "end": v(1.24, 11.56) * mm});
            skLineSegment(sketch, "E24.44.1", {"start": v(0.84, 10.55) * mm, "end": v(1.24, 11.56) * mm});
            skLineSegment(sketch, "E24.44.2", {"start": v(2.1, 10.37) * mm, "end": v(2, 11.45) * mm});
            skArc(sketch, "E24.44.3", {"start": v(0.71, 10.48) * mm, "mid": v(0.8, 10.5) * mm, "end": v(0.84, 10.56) * mm});
            skArc(sketch, "E24.44.4", {"start": v(2.2, 10.27) * mm, "mid": v(2.14, 10.3) * mm, "end": v(2.1, 10.37) * mm});
            skSolve(sketch);
        }
        {
            var Q0;
            Q0=makeQuery(id+"F4.imprint","IMPRINT",FACE,{"disambiguationData":[TD([[makeQuery(id+"F4.imprint","IMPRINT",EDGE,{"derivedFrom":sQuery(id+"F4.wireOp",EDGE,"E16")}),-1.0]])]});
            var Q1;
            Q1=makeQuery(id+"F4.imprint","IMPRINT",FACE,{"disambiguationData":[TD([[makeQuery(id+"F4.imprint","IMPRINT",EDGE,{"derivedFrom":sQuery(id+"F4.wireOp",EDGE,"E19.0")}),-1.0]])]});
            extrude(context, id + "F5", {"entities" : qUnion([Q0, Q1]), "operationType" : NewBodyOperationType.REMOVE, "endBound" : BoundingType.THROUGH_ALL, "oppositeDirection" : true, "depth" : 25 * mm});
        }
        {
            var Q0;
            Q0=makeQuery(id+"F1.opExtrude","CAP_FACE",FACE,{"disambiguationData":[OSD([sQuery(id+"F0.wireOp",EDGE,"E1"),sQuery(id+"F0.wireOp",EDGE,"E2"),sQuery(id+"F0.wireOp",EDGE,"E3"),sQuery(id+"F0.wireOp",EDGE,"E4"),sQuery(id+"F0.wireOp",EDGE,"E5"),sQuery(id+"F0.wireOp",EDGE,"E6"),sQuery(id+"F0.wireOp",EDGE,"E7"),sQuery(id+"F0.wireOp",EDGE,"E8"),sQuery(id+"F0.wireOp",EDGE,"E9"),sQuery(id+"F0.wireOp",EDGE,"E10")])],"isStart":false});
            var sketch = newSketch(context, id + "F6", { "sketchPlane" : qUnion([Q0])});
            skArc(sketch, "E25.0", {"start": v(-3.97, 3.2) * mm, "mid": v(-5.1, 0) * mm, "end": v(-3.97, -3.2) * mm});
            skArc(sketch, "E25.1", {"start": v(3.2, 3.97) * mm, "mid": v(0, 5.1) * mm, "end": v(-3.2, 3.97) * mm});
            skArc(sketch, "E25.2", {"start": v(3.97, -3.2) * mm, "mid": v(5.1, 0) * mm, "end": v(3.97, 3.2) * mm});
            skArc(sketch, "E25.3", {"start": v(-3.2, -3.97) * mm, "mid": v(0, -5.1) * mm, "end": v(3.2, -3.97) * mm});
            skCircle(sketch, "E25.4", {"center": v(4.88, -4.88) * mm, "radius": 0.94 * mm});
            skCircle(sketch, "E25.5", {"center": v(-4.88, -4.88) * mm, "radius": 0.94 * mm});
            skCircle(sketch, "E25.6", {"center": v(-4.88, 4.88) * mm, "radius": 0.94 * mm});
            skCircle(sketch, "E25.7", {"center": v(4.88, 4.88) * mm, "radius": 0.94 * mm});
            skArc(sketch, "E26", {"start": v(3.2, -3.97) * mm, "mid": v(3.53, -3.53) * mm, "end": v(3.97, -3.2) * mm});
            skArc(sketch, "E27", {"start": v(3.97, 3.2) * mm, "mid": v(3.53, 3.53) * mm, "end": v(3.2, 3.97) * mm});
            skArc(sketch, "E28", {"start": v(-3.2, 3.97) * mm, "mid": v(-3.53, 3.53) * mm, "end": v(-3.97, 3.2) * mm});
            skArc(sketch, "E29", {"start": v(-3.97, -3.2) * mm, "mid": v(-3.53, -3.53) * mm, "end": v(-3.2, -3.97) * mm});
            skCircle(sketch, "E30.0", {"center": v(0, 0) * mm, "radius": 4.03 * mm});
            skSolve(sketch);
        }
        {
            var Q0;
            Q0 = qSketchRegion(id + "F6", true);
            extrude(context, id + "F7", {"entities" : qUnion([Q0]), "operationType" : NewBodyOperationType.REMOVE, "oppositeDirection" : true, "depth" : 1.25 * mm});
        }
        {
            var Q0;
            Q0=makeQuery(id+"F3.opExtrude","CAP_FACE",FACE,{"disambiguationData":[OSD([sQuery(id+"F2.wireOp",EDGE,"E11")])],"isStart":true});
            var sketch = newSketch(context, id + "F8", { "sketchPlane" : qUnion([Q0])});
            skCircle(sketch, "E31.0", {"center": v(0, 0) * mm, "radius": 4.03 * mm});
            skSolve(sketch);
        }
        {
            var Q0;
            Q0 = qSketchRegion(id + "F8", true);
            extrude(context, id + "F9", {"entities" : qUnion([Q0]), "operationType" : NewBodyOperationType.REMOVE, "endBound" : BoundingType.THROUGH_ALL, "oppositeDirection" : true, "depth" : 25 * mm});
        }
    });
